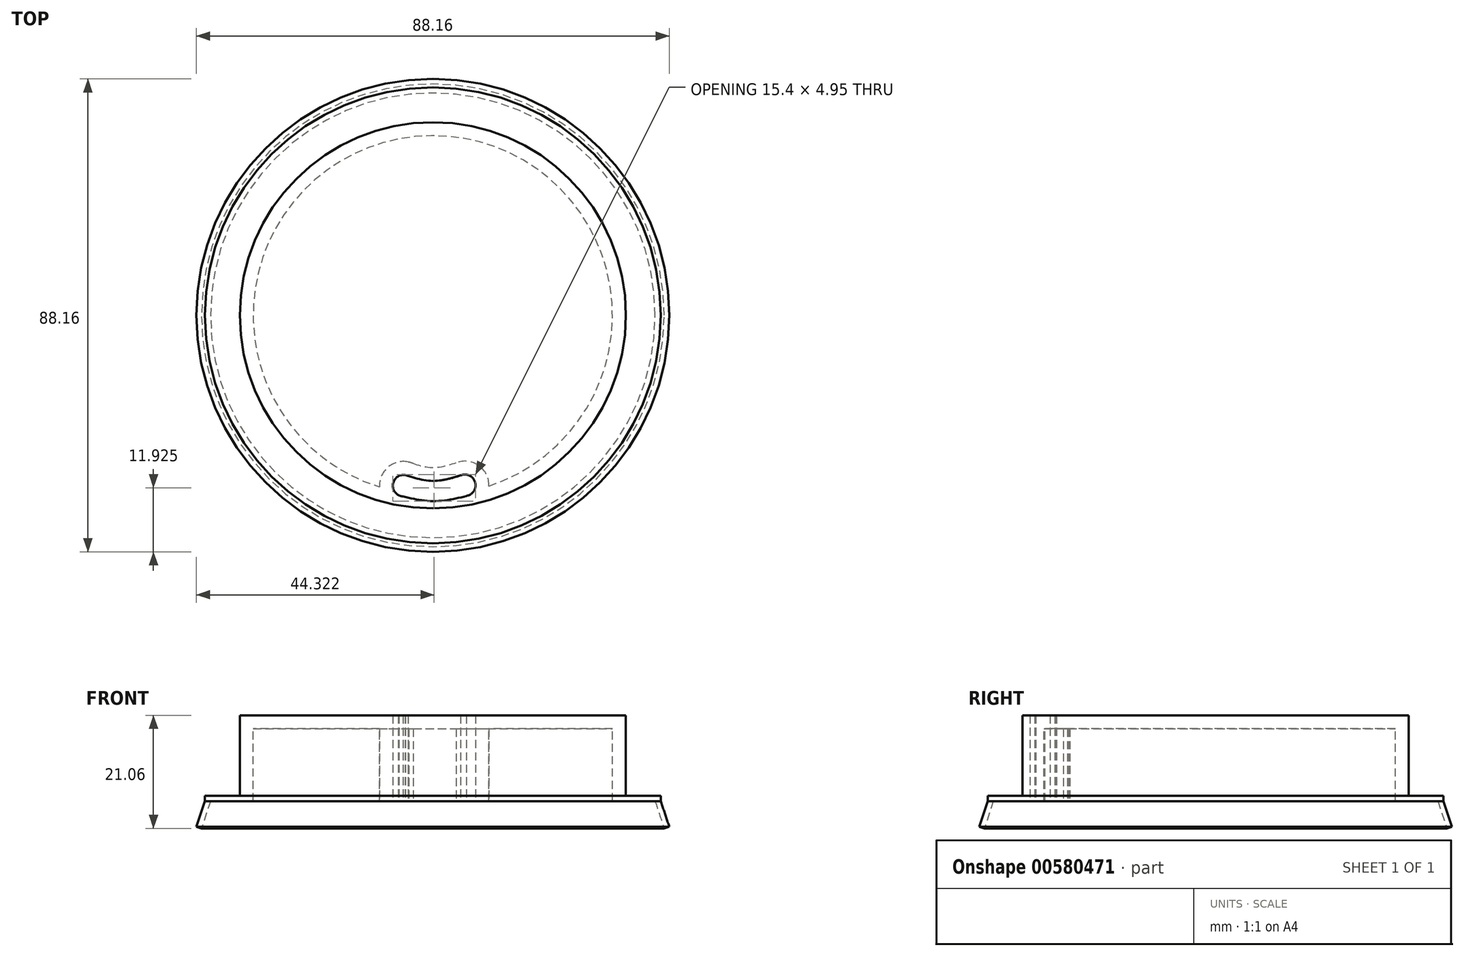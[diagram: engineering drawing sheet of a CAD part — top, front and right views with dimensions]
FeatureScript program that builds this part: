
annotation { "Feature Type Name" : "Feature", "Feature Type Description" : "" }
export const myFeature = defineFeature(function(context is Context, id is Id, definition is map)
    precondition{}
    {
        {
            var Q0;
            Q0=qCreatedBy(makeId("Front.planeOp"),FACE);
            var sketch = newSketch(context, id + "F0", { "sketchPlane" : qUnion([Q0])});
            skLineSegment(sketch, "E0", {"start": v(0, 0) * mm, "end": v(42.5, 0) * mm});
            skLineSegment(sketch, "E1", {"start": v(42.5, 0) * mm, "end": v(44.08, -4.74) * mm});
            skLineSegment(sketch, "E2", {"start": v(44.08, -4.74) * mm, "end": v(43.13, -5.06) * mm});
            skLineSegment(sketch, "E3", {"start": v(43.13, -5.06) * mm, "end": v(41.45, 0) * mm});
            skLineSegment(sketch, "E4", {"start": v(42.5, 0) * mm, "end": v(42.5, 1) * mm});
            skLineSegment(sketch, "E5", {"start": v(42.5, 1) * mm, "end": v(0, 1) * mm});
            skLineSegment(sketch, "E6", {"start": v(36, 1) * mm, "end": v(36, 16) * mm});
            skLineSegment(sketch, "E7", {"start": v(36, 16) * mm, "end": v(0, 16) * mm});
            skLineSegment(sketch, "E8", {"start": v(0, 16) * mm, "end": v(0, 1) * mm});
            skLineSegment(sketch, "E9", {"start": v(0, 1) * mm, "end": v(0, 0) * mm});
            skSolve(sketch);
        }
        {
            var Q0;
            {var subQ2=sQuery(id+"F0.wireOp",EDGE,"E6");Q0=makeQuery(id+"F0.imprint","IMPRINT",FACE,{"disambiguationData":[TD([[makeQuery(id+"F0.imprint","IMPRINT",EDGE,{"derivedFrom":subQ2}),1.0]])]});}
            var Q1;
            {var subQ1=sQuery(id+"F0.wireOp",EDGE,"E4");Q1=makeQuery(id+"F0.imprint","IMPRINT",FACE,{"disambiguationData":[TD([[makeQuery(id+"F0.imprint","IMPRINT",EDGE,{"derivedFrom":subQ1}),1.0]])]});}
            var Q2;
            {var subQ0=sQuery(id+"F0.wireOp",EDGE,"E1");Q2=makeQuery(id+"F0.imprint","IMPRINT",FACE,{"disambiguationData":[TD([[makeQuery(id+"F0.imprint","IMPRINT",EDGE,{"derivedFrom":subQ0}),-1.0]])]});}
            var Q3;
            Q3=sQuery(id+"F0.wireOp",EDGE,"E8");
            revolve(context, id + "F1", {"entities" : qUnion([Q0, Q1, Q2]), "axis" : qUnion([Q3]), "revolveType" : RevolveType.FULL});
        }
        {
            var Q0;
            Q0=qCreatedBy(makeId("Top.planeOp"),FACE);
            var sketch = newSketch(context, id + "F2", { "sketchPlane" : qUnion([Q0])});
            skArc(sketch, "E10", {"start": v(-5.2, -29.75) * mm, "mid": v(-7.36, -31.14) * mm, "end": v(-6.42, -33.52) * mm});
            skFitSpline(sketch, "E11", {"points": [v(-5.2, -29.75) * mm, v(0, -30.86) * mm, v(5.47, -29.75) * mm], "startDerivative": vector(10.48, -3.35) * mm, "endDerivative": vector(10.9, 3.33) * mm});
            skFitSpline(sketch, "E12", {"points": [v(-6.42, -33.52) * mm, v(0, -34.63) * mm, v(6.73, -33.52) * mm], "startDerivative": vector(12.9, -3.44) * mm, "endDerivative": vector(11.38, 3.53) * mm});
            skArc(sketch, "E13", {"start": v(6.73, -33.52) * mm, "mid": v(7.85, -31.05) * mm, "end": v(5.47, -29.75) * mm});
            skSolve(sketch);
        }
        {
            var Q0;
            Q0=sQuery(id+"F2.wireOp",VERTEX,"E10.center");
            var Q1;
            Q1=makeQuery(id+"F1.opRevolve","SWEPT_BODY",BODY,{"disambiguationData":[OSD([sQuery(id+"F0.wireOp",EDGE,"E0"),sQuery(id+"F0.wireOp",EDGE,"E1"),sQuery(id+"F0.wireOp",EDGE,"E2"),sQuery(id+"F0.wireOp",EDGE,"E3"),sQuery(id+"F0.wireOp",EDGE,"E4"),sQuery(id+"F0.wireOp",EDGE,"E5"),sQuery(id+"F0.wireOp",EDGE,"E6"),sQuery(id+"F0.wireOp",EDGE,"E7"),sQuery(id+"F0.wireOp",EDGE,"E8"),sQuery(id+"F0.wireOp",EDGE,"E9")])]});
            hole(context, id + "F3", {"style" : HoleStyle.SIMPLE, "endStyle" : HoleEndStyle.THROUGH, "oppositeDirection" : true, "holeDiameter" : 4 * mm, "isTappedThrough" : true, "tappedDepth" : 12 * mm, "tapClearance" : 3, "locations" : qUnion([Q0]), "scope" : qUnion([Q1])});
        }
        {
            var Q0;
            Q0=sQuery(id+"F2.wireOp",VERTEX,"E13.center");
            var Q1;
            Q1=makeQuery(id+"F1.opRevolve","SWEPT_BODY",BODY,{"disambiguationData":[OSD([sQuery(id+"F0.wireOp",EDGE,"E0"),sQuery(id+"F0.wireOp",EDGE,"E1"),sQuery(id+"F0.wireOp",EDGE,"E2"),sQuery(id+"F0.wireOp",EDGE,"E3"),sQuery(id+"F0.wireOp",EDGE,"E4"),sQuery(id+"F0.wireOp",EDGE,"E5"),sQuery(id+"F0.wireOp",EDGE,"E6"),sQuery(id+"F0.wireOp",EDGE,"E7"),sQuery(id+"F0.wireOp",EDGE,"E8"),sQuery(id+"F0.wireOp",EDGE,"E9")])]});
            hole(context, id + "F4", {"style" : HoleStyle.SIMPLE, "endStyle" : HoleEndStyle.THROUGH, "oppositeDirection" : true, "holeDiameter" : 4 * mm, "isTappedThrough" : true, "tappedDepth" : 12 * mm, "tapClearance" : 3, "locations" : qUnion([Q0]), "scope" : qUnion([Q1])});
        }
        {
            var Q0;
            Q0=makeQuery(id+"F2.imprint","IMPRINT",FACE,{"disambiguationData":[TD([[makeQuery(id+"F2.imprint","IMPRINT",EDGE,{"derivedFrom":sQuery(id+"F2.wireOp",EDGE,"E10")}),1.0]])]});
            extrude(context, id + "F5", {"entities" : qUnion([Q0]), "operationType" : NewBodyOperationType.REMOVE, "depth" : 110 * mm, "offsetDistance" : 25 * mm});
        }
        {
            var Q0;
            Q0=makeQuery(id+"F1.opRevolve","SWEPT_FACE",FACE,{"disambiguationData":[OSD([sQuery(id+"F0.wireOp",EDGE,"E0")])]});
            shell(context, id + "F6", {"entities" : qUnion([Q0]), "thickness" : 2.5 * mm});
        }
    });
